# Revit family: D2DTYP004
name_source: partatom
category: Furniture
units: mm (PartAtom-declared; Revit-internal decimal feet)

## family parameters
Always vertical = Yes
Cut with Voids When Loaded = No
OmniClass Number = 23.40.20.00
OmniClass Title = General Furniture and Specialties
Render Appearance Source = Family Geometry
Room Calculation Point = No
Shared = No
Work Plane-Based = No

## types (1)
- D2DTYP004
    Cost = 4797 $
    Default Elevation = 0 mm  [stored 0 ft]
    Description = 2 x Pierce Side Chair on Glides, Blue Back/Fabric Gray Frame, 2 x Pierce Stool Blue Back/fabric Choice Seat Gray Frame, 1 x Pack fee per Chair is less than multiple of 3, 1 x Tbl, Rnd, 2mm, 36dx29h, Stlx36, Gld, 1 x Tbl, Rnd, 2mm, 36dx42h, Stlx36, Gld
    Exported From CET Designer = Yes
    Manufacturer = AIS
    Model = 3500CBU
    Show D2DTYP004 = Yes
    VisibilityIndex = 0

note: [stored X ft] marks values corroborated as IEEE doubles in the binary element streams (Revit-internal decimal feet)

## geometry (parser evidence)
native form markers: Sweep x3
no freeform markers — native parametric forms only
